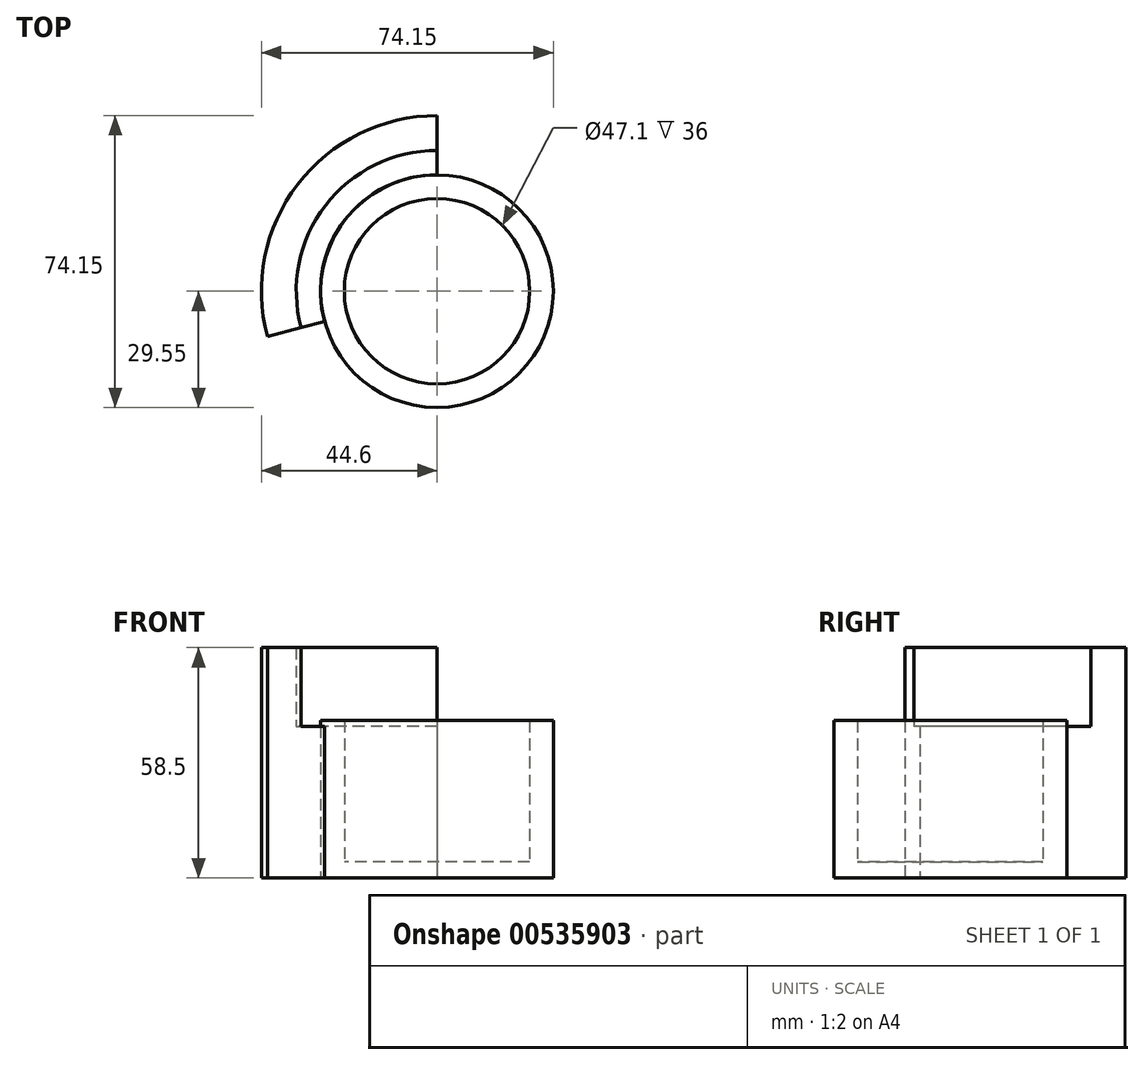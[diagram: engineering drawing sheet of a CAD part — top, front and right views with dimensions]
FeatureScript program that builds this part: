
annotation { "Feature Type Name" : "Feature", "Feature Type Description" : "" }
export const myFeature = defineFeature(function(context is Context, id is Id, definition is map)
    precondition{}
    {
        {
            var Q0;
            Q0=qCreatedBy(makeId("Top.planeOp"),FACE);
            var sketch = newSketch(context, id + "F0", { "sketchPlane" : qUnion([Q0])});
            skCircle(sketch, "E0", {"center": v(0, 0) * mm, "radius": 29.55 * mm});
            skSolve(sketch);
        }
        {
            var Q0;
            Q0=makeQuery(id+"F0.imprint","IMPRINT",FACE,{"disambiguationData":[TD([[makeQuery(id+"F0.imprint","IMPRINT",EDGE,{"derivedFrom":sQuery(id+"F0.wireOp",EDGE,"E0")}),1.0]])]});
            extrude(context, id + "F1", {"entities" : qUnion([Q0]), "depth" : 4 * mm, "offsetDistance" : 25 * mm});
        }
        {
            var Q0;
            Q0=makeQuery(id+"F1.opExtrude","CAP_FACE",FACE,{"disambiguationData":[OSD([sQuery(id+"F0.wireOp",EDGE,"E0")])],"isStart":false});
            var sketch = newSketch(context, id + "F2", { "sketchPlane" : qUnion([Q0])});
            skCircle(sketch, "E1", {"center": v(0, 0) * mm, "radius": 23.55 * mm});
            skSolve(sketch);
        }
        {
            var Q0;
            Q0=makeQuery(id+"F2.imprint","IMPRINT",FACE,{"disambiguationData":[TD([[makeQuery(id+"F2.imprint","IMPRINT",EDGE,{"derivedFrom":sQuery(id+"F2.wireOp",EDGE,"E1")}),-1.0]])]});
            extrude(context, id + "F3", {"entities" : qUnion([Q0]), "operationType" : NewBodyOperationType.ADD, "depth" : 36 * mm, "offsetDistance" : 25 * mm});
        }
        {
            var Q0;
            Q0=qCreatedBy(makeId("Top.planeOp"),FACE);
            var sketch = newSketch(context, id + "F4", { "sketchPlane" : qUnion([Q0])});
            skCircle(sketch, "E2", {"center": v(0, 0) * mm, "radius": 29.6 * mm});
            skCircle(sketch, "E3", {"center": v(0, 0) * mm, "radius": 44.6 * mm});
            skLineSegment(sketch, "E4", {"start": v(0, 0) * mm, "end": v(0, 44.6) * mm});
            skLineSegment(sketch, "E5.1.0", {"start": v(0, 0) * mm, "end": v(-38.62, -22.3) * mm});
            skLineSegment(sketch, "E5.2.0", {"start": v(0, 0) * mm, "end": v(38.62, -22.3) * mm});
            skLineSegment(sketch, "E6", {"start": v(0, 0) * mm, "end": v(11.54, 43.08) * mm});
            skLineSegment(sketch, "E7.1.0", {"start": v(0, 0) * mm, "end": v(-43.08, -11.54) * mm});
            skLineSegment(sketch, "E7.2.0", {"start": v(0, 0) * mm, "end": v(31.54, -31.54) * mm});
            skCircle(sketch, "E8", {"center": v(0, 0) * mm, "radius": 35.75 * mm});
            skSolve(sketch);
        }
        {
            var Q0;
            {var subQ0=sQuery(id+"F4.wireOp",EDGE,"E4");var subQ1=sQuery(id+"F4.wireOp",EDGE,"E2");var subQ2=makeQuery(id+"F4.imprint","INTERSECT",VERTEX,{"derivedFrom":[subQ1,subQ0]});Q0=makeQuery(id+"F4.imprint","IMPRINT",FACE,{"disambiguationData":[TD([[makeQuery(id+"F4.imprint","IMPRINT",EDGE,{"disambiguationData":[TD([[subQ2,-1.0]])],"derivedFrom":subQ1}),-1.0]])]});}
            extrude(context, id + "F5", {"entities" : qUnion([Q0]), "depth" : 38.5 * mm, "offsetDistance" : 25 * mm});
        }
        {
            var Q0;
            {var subQ0=sQuery(id+"F4.wireOp",EDGE,"E4");var subQ1=sQuery(id+"F4.wireOp",EDGE,"E3");var subQ2=makeQuery(id+"F4.imprint","INTERSECT",VERTEX,{"derivedFrom":[subQ1,subQ0]});Q0=makeQuery(id+"F4.imprint","IMPRINT",FACE,{"disambiguationData":[TD([[makeQuery(id+"F4.imprint","IMPRINT",EDGE,{"disambiguationData":[TD([[subQ2,-1.0]])],"derivedFrom":subQ1}),1.0]])]});}
            extrude(context, id + "F6", {"entities" : qUnion([Q0]), "operationType" : NewBodyOperationType.ADD, "depth" : (38.5 + 20) * mm, "offsetDistance" : 25 * mm});
        }
    });
